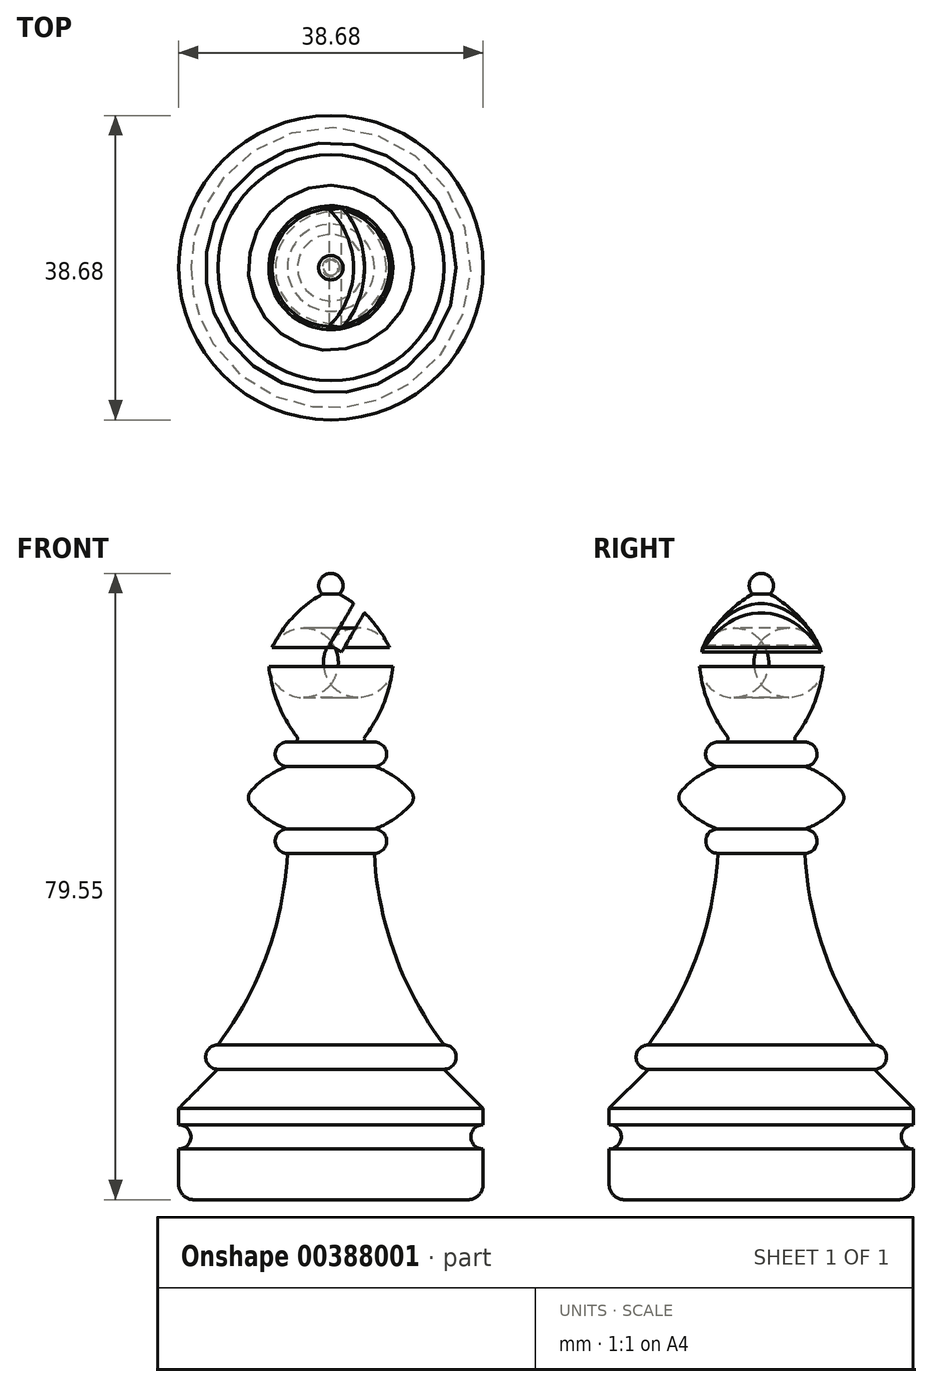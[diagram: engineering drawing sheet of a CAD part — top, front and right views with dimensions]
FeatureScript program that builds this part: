
annotation { "Feature Type Name" : "Feature", "Feature Type Description" : "" }
export const myFeature = defineFeature(function(context is Context, id is Id, definition is map)
    precondition{}
    {
        {
            var Q0;
            Q0=qCreatedBy(makeId("Front.planeOp"),FACE);
            var sketch = newSketch(context, id + "F0", { "sketchPlane" : qUnion([Q0])});
            skLineSegment(sketch, "E0", {"start": v(0, 0) * mm, "end": v(16.51, 0) * mm});
            skLineSegment(sketch, "E1", {"start": v(16.51, 0) * mm, "end": v(22.22, -5.71) * mm});
            skLineSegment(sketch, "E2", {"start": v(22.22, -5.71) * mm, "end": v(22.22, -8.1) * mm});
            skArc(sketch, "E3", {"start": v(22.23, -8.1) * mm, "mid": v(20.45, -9.88) * mm, "end": v(22.22, -11.66) * mm});
            skLineSegment(sketch, "E4", {"start": v(22.23, -11.66) * mm, "end": v(22.23, -19.05) * mm});
            skLineSegment(sketch, "E5", {"start": v(22.23, -19.05) * mm, "end": v(0, -19.05) * mm});
            skLineSegment(sketch, "E6", {"start": v(0, -19.05) * mm, "end": v(0, 0) * mm});
            skSolve(sketch);
        }
        {
            var Q0;
            Q0=makeQuery(id+"F0.imprint","IMPRINT",FACE,{"disambiguationData":[TD([[makeQuery(id+"F0.imprint","IMPRINT",EDGE,{"derivedFrom":sQuery(id+"F0.wireOp",EDGE,"E0")}),-1.0]])]});
            var Q1;
            Q1=sQuery(id+"F0.wireOp",EDGE,"E6");
            revolve(context, id + "F1", {"entities" : qUnion([Q0]), "axis" : qUnion([Q1]), "revolveType" : RevolveType.FULL});
        }
        {
            var Q0;
            Q0=makeQuery(id+"F1.opRevolve","SWEPT_EDGE",EDGE,{"disambiguationData":[OSD([sQuery(id+"F0.wireOp",EDGE,"E4"),sQuery(id+"F0.wireOp",EDGE,"E5")])]});
            fillet(context, id + "F2", {"entities" : qUnion([Q0]), "radius" : 2.22 * mm, "tangentPropagation" : true, "defaultsChanged" : true, "vertexSettings" : [], "allowEdgeOverflow" : false});
        }
        {
            var Q0;
            Q0=qCreatedBy(makeId("Front.planeOp"),FACE);
            var sketch = newSketch(context, id + "F3", { "sketchPlane" : qUnion([Q0])});
            skLineSegment(sketch, "E7", {"start": v(0, 72.4) * mm, "end": v(0, 0) * mm});
            skLineSegment(sketch, "E8", {"start": v(0, 0) * mm, "end": v(16.51, 0) * mm});
            skArc(sketch, "E9", {"start": v(16.51, 0) * mm, "mid": v(18.29, 1.78) * mm, "end": v(16.51, 3.56) * mm});
            skArc(sketch, "E10", {"start": v(6.35, 31.52) * mm, "mid": v(9.34, 16.78) * mm, "end": v(16.51, 3.56) * mm});
            skArc(sketch, "E11", {"start": v(6.35, 31.52) * mm, "mid": v(8.13, 33.3) * mm, "end": v(6.35, 35.08) * mm});
            skArc(sketch, "E12", {"start": v(6.35, 35.08) * mm, "mid": v(9.75, 36.9) * mm, "end": v(12.45, 39.65) * mm});
            skArc(sketch, "E13", {"start": v(12.45, 39.65) * mm, "mid": v(9.75, 42.4) * mm, "end": v(6.35, 44.22) * mm});
            skArc(sketch, "E14", {"start": v(6.35, 44.22) * mm, "mid": v(8.13, 46) * mm, "end": v(6.35, 47.78) * mm});
            skArc(sketch, "E15", {"start": v(9.14, 60.22) * mm, "mid": v(6, 65.48) * mm, "end": v(1.27, 69.37) * mm});
            skArc(sketch, "E16", {"start": v(1.27, 69.37) * mm, "mid": v(1.64, 71.3) * mm, "end": v(0, 72.4) * mm});
            skLineSegment(sketch, "E17", {"start": v(6.35, 35.08) * mm, "end": v(6.35, 44.22) * mm, "construction": true});
            skLineSegment(sketch, "E18", {"start": v(6.35, 39.65) * mm, "end": v(12.45, 39.65) * mm, "construction": true});
            skArc(sketch, "E19", {"start": v(4.32, 47.78) * mm, "mid": v(7.78, 53.6) * mm, "end": v(9.14, 60.22) * mm});
            skLineSegment(sketch, "E20", {"start": v(4.32, 47.78) * mm, "end": v(6.35, 47.78) * mm});
            skPoint(sketch, "E21", {"position": v(4.12, 67.37) * mm});
            skLineSegment(sketch, "E22", {"start": v(4.12, 67.37) * mm, "end": v(0, 60.22) * mm, "construction": true});
            skSolve(sketch);
        }
        {
            var Q0;
            Q0 = qSketchRegion(id + "F3", true);
            var Q1;
            Q1=sQuery(id+"F3.wireOp",EDGE,"E7");
            revolve(context, id + "F4", {"operationType" : NewBodyOperationType.ADD, "entities" : qUnion([Q0]), "axis" : qUnion([Q1]), "revolveType" : RevolveType.FULL});
        }
        {
            var Q0;
            Q0=makeQuery(id+"F4.opRevolve","SWEPT_EDGE",EDGE,{"disambiguationData":[OSD([sQuery(id+"F3.wireOp",EDGE,"E15"),sQuery(id+"F3.wireOp",EDGE,"E19")])]});
            fillet(context, id + "F5", {"entities" : qUnion([Q0]), "radius" : 5.08 * mm, "tangentPropagation" : true, "allowEdgeOverflow" : false});
        }
        {
            var Q0;
            Q0=makeQuery(id+"F4.opRevolve","SWEPT_EDGE",EDGE,{"disambiguationData":[OSD([sQuery(id+"F3.wireOp",EDGE,"E19"),sQuery(id+"F3.wireOp",EDGE,"E20")])]});
            fillet(context, id + "F6", {"entities" : qUnion([Q0]), "radius" : 0.5 * mm, "tangentPropagation" : true, "allowEdgeOverflow" : false});
        }
        {
            var Q0;
            Q0=sQuery(id+"F3.wireOp",VERTEX,"E21");
            var Q1;
            Q1=sQuery(id+"F3.wireOp",EDGE,"E22");
            cPlane(context, id + "F7", {"entities" : qUnion([Q0, Q1]), "cplaneType" : CPlaneType.LINE_POINT, "offset" : 25.4 * mm, "width" : 152.4 * mm, "height" : 152.4 * mm});
        }
        {
            var Q0;
            Q0=qCreatedBy(id+"F7.planeOp",FACE);
            var sketch = newSketch(context, id + "F8", { "sketchPlane" : qUnion([Q0])});
            skLineSegment(sketch, "E23.bottom", {"start": v(-29.1, 12.7) * mm, "end": v(-31.13, 12.7) * mm});
            skLineSegment(sketch, "E23.top", {"start": v(-29.1, -12.7) * mm, "end": v(-31.13, -12.7) * mm});
            skLineSegment(sketch, "E23.left", {"start": v(-29.1, 12.7) * mm, "end": v(-29.1, -12.7) * mm});
            skLineSegment(sketch, "E23.right", {"start": v(-31.13, 12.7) * mm, "end": v(-31.13, -12.7) * mm});
            skPoint(sketch, "E23.middle", {"position": v(-30.11, 0) * mm});
            skSolve(sketch);
        }
        {
            var Q0;
            Q0 = qSketchRegion(id + "F8", true);
            var Q1;
            Q1=qCreatedBy(id+"FaZgaIPp9X6yMJz_1.planeOp",FACE);
            extrude(context, id + "F9", {"entities" : qUnion([Q0]), "operationType" : NewBodyOperationType.REMOVE, "oppositeDirection" : true, "depth" : 2.54 * mm, "hasSecondDirection" : true, "secondDirectionOppositeDirection" : false, "secondDirectionBoundEntityFace" : qUnion([Q1]), "secondDirectionDepth" : 6.86 * mm});
        }
        {
            var Q0;
            Q0=makeQuery(id+"F1.opRevolve","SWEPT_BODY",BODY,{"disambiguationData":[OSD([sQuery(id+"F0.wireOp",EDGE,"E0"),sQuery(id+"F0.wireOp",EDGE,"E1"),sQuery(id+"F0.wireOp",EDGE,"E2"),sQuery(id+"F0.wireOp",EDGE,"E3"),sQuery(id+"F0.wireOp",EDGE,"E4"),sQuery(id+"F0.wireOp",EDGE,"E5"),sQuery(id+"F0.wireOp",EDGE,"E6")])]});
            var Q1;
            Q1=qCreatedBy(makeId("Origin.pointOp"),VERTEX);
            transform(context, id + "F10", {"entities" : qUnion([Q0]), "transformType" : TransformType.SCALE_UNIFORMLY, "scale" : .87, "scalePoint" : qUnion([Q1]), "makeCopy" : false});
        }
        {
            var Q0;
            Q0=makeQuery(id+"F4.opRevolve","SWEPT_EDGE",EDGE,{"disambiguationData":[OSD([sQuery(id+"F3.wireOp",EDGE,"E12"),sQuery(id+"F3.wireOp",EDGE,"E13")])]});
            fillet(context, id + "F11", {"entities" : qUnion([Q0]), "radius" : 1.27 * mm, "tangentPropagation" : true, "allowEdgeOverflow" : false});
        }
    });
